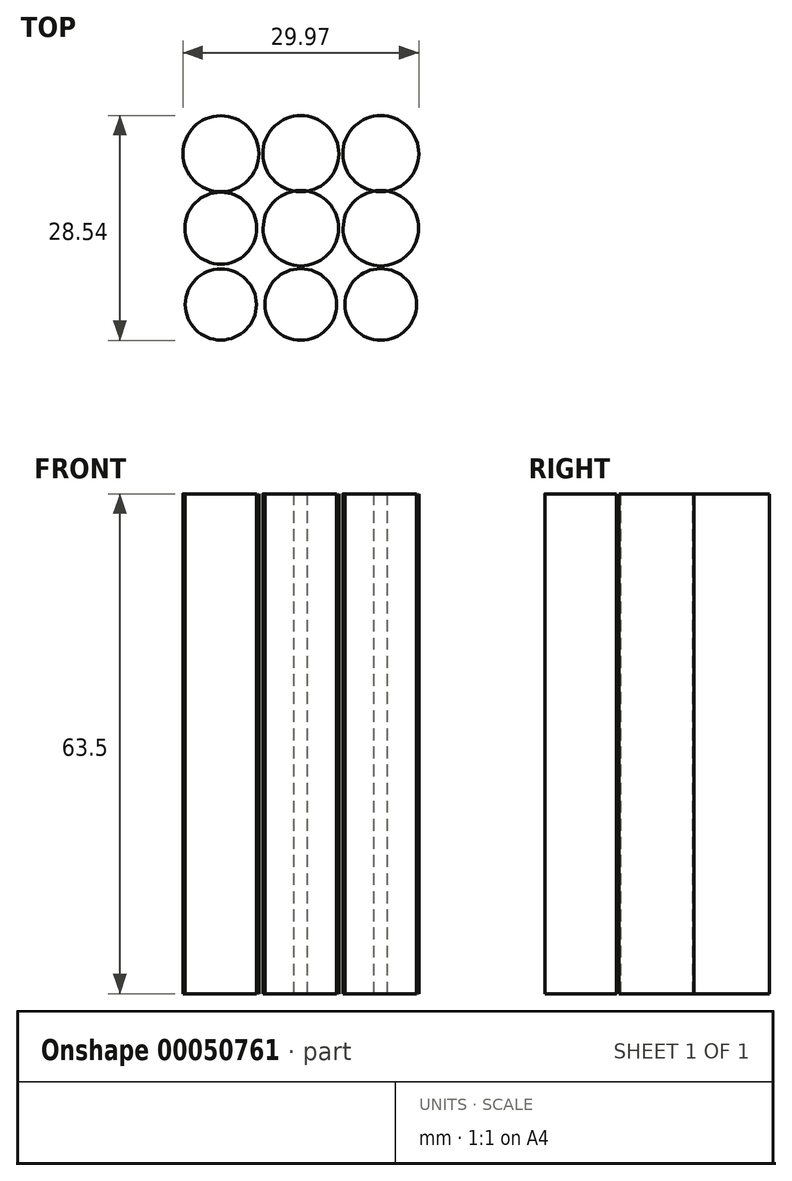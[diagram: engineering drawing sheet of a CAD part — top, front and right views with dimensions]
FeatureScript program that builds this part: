
annotation { "Feature Type Name" : "Feature", "Feature Type Description" : "" }
export const myFeature = defineFeature(function(context is Context, id is Id, definition is map)
    precondition{}
    {
        {
            var Q0;
            Q0=qCreatedBy(makeId("Top.planeOp"),FACE);
            var sketch = newSketch(context, id + "F0", { "sketchPlane" : qUnion([Q0])});
            skCircle(sketch, "E0", {"center": v(-37.18, 37.5) * mm, "radius": 4.83 * mm});
            skCircle(sketch, "E1", {"center": v(-27.02, 37.5) * mm, "radius": 4.83 * mm});
            skCircle(sketch, "E2", {"center": v(-16.86, 37.5) * mm, "radius": 4.83 * mm});
            skCircle(sketch, "E3", {"center": v(-37.18, 28.05) * mm, "radius": 4.57 * mm});
            skCircle(sketch, "E4", {"center": v(-27.02, 28.05) * mm, "radius": 4.79 * mm});
            skCircle(sketch, "E5", {"center": v(-16.86, 28.05) * mm, "radius": 4.79 * mm});
            skCircle(sketch, "E6", {"center": v(-37.18, 18.35) * mm, "radius": 4.52 * mm});
            skCircle(sketch, "E7", {"center": v(-27.02, 18.35) * mm, "radius": 4.55 * mm});
            skCircle(sketch, "E8", {"center": v(-16.86, 18.35) * mm, "radius": 4.54 * mm});
            skSolve(sketch);
        }
        {
            var Q0;
            Q0=makeQuery(id+"F0.imprint","IMPRINT",FACE,{"disambiguationData":[TD([[makeQuery(id+"F0.imprint","IMPRINT",EDGE,{"derivedFrom":sQuery(id+"F0.wireOp",EDGE,"E6")}),1.0]])]});
            var Q1;
            Q1=makeQuery(id+"F0.imprint","IMPRINT",FACE,{"disambiguationData":[TD([[makeQuery(id+"F0.imprint","IMPRINT",EDGE,{"derivedFrom":sQuery(id+"F0.wireOp",EDGE,"E7")}),1.0]])]});
            var Q2;
            Q2=makeQuery(id+"F0.imprint","IMPRINT",FACE,{"disambiguationData":[TD([[makeQuery(id+"F0.imprint","IMPRINT",EDGE,{"derivedFrom":sQuery(id+"F0.wireOp",EDGE,"E8")}),1.0]])]});
            var Q3;
            {var subQ0=sQuery(id+"F0.wireOp",EDGE,"E5");var subQ1=sQuery(id+"F0.wireOp",EDGE,"E2");var subQ2=makeQuery(id+"F0.imprint","INTERSECT",VERTEX,{"disambiguationData":[OD(0.0)],"derivedFrom":[subQ1,subQ0]});Q3=makeQuery(id+"F0.imprint","IMPRINT",FACE,{"disambiguationData":[TD([[makeQuery(id+"F0.imprint","IMPRINT",EDGE,{"disambiguationData":[TD([[subQ2,-1.0]])],"derivedFrom":subQ1}),-1.0]])]});}
            var Q4;
            {var subQ0=sQuery(id+"F0.wireOp",EDGE,"E4");var subQ1=sQuery(id+"F0.wireOp",EDGE,"E1");var subQ2=makeQuery(id+"F0.imprint","INTERSECT",VERTEX,{"disambiguationData":[OD(0.0)],"derivedFrom":[subQ1,subQ0]});Q4=makeQuery(id+"F0.imprint","IMPRINT",FACE,{"disambiguationData":[TD([[makeQuery(id+"F0.imprint","IMPRINT",EDGE,{"disambiguationData":[TD([[subQ2,-1.0]])],"derivedFrom":subQ1}),-1.0]])]});}
            var Q5;
            Q5=makeQuery(id+"F0.imprint","IMPRINT",FACE,{"disambiguationData":[TD([[makeQuery(id+"F0.imprint","IMPRINT",EDGE,{"derivedFrom":sQuery(id+"F0.wireOp",EDGE,"E3")}),1.0]])]});
            var Q6;
            Q6=makeQuery(id+"F0.imprint","IMPRINT",FACE,{"disambiguationData":[TD([[makeQuery(id+"F0.imprint","IMPRINT",EDGE,{"derivedFrom":sQuery(id+"F0.wireOp",EDGE,"E0")}),1.0]])]});
            var Q7;
            {var subQ0=sQuery(id+"F0.wireOp",EDGE,"E4");var subQ1=sQuery(id+"F0.wireOp",EDGE,"E1");var subQ2=makeQuery(id+"F0.imprint","INTERSECT",VERTEX,{"disambiguationData":[OD(0.0)],"derivedFrom":[subQ1,subQ0]});Q7=makeQuery(id+"F0.imprint","IMPRINT",FACE,{"disambiguationData":[TD([[makeQuery(id+"F0.imprint","IMPRINT",EDGE,{"disambiguationData":[TD([[subQ2,1.0]])],"derivedFrom":subQ1}),1.0]])]});}
            var Q8;
            {var subQ0=sQuery(id+"F0.wireOp",EDGE,"E5");var subQ1=sQuery(id+"F0.wireOp",EDGE,"E2");var subQ2=makeQuery(id+"F0.imprint","INTERSECT",VERTEX,{"disambiguationData":[OD(0.0)],"derivedFrom":[subQ1,subQ0]});Q8=makeQuery(id+"F0.imprint","IMPRINT",FACE,{"disambiguationData":[TD([[makeQuery(id+"F0.imprint","IMPRINT",EDGE,{"disambiguationData":[TD([[subQ2,1.0]])],"derivedFrom":subQ1}),1.0]])]});}
            extrude(context, id + "F1", {"entities" : qUnion([Q0, Q1, Q2, Q3, Q4, Q5, Q6, Q7, Q8]), "oppositeDirection" : true, "depth" : 63.5 * mm});
        }
    });
